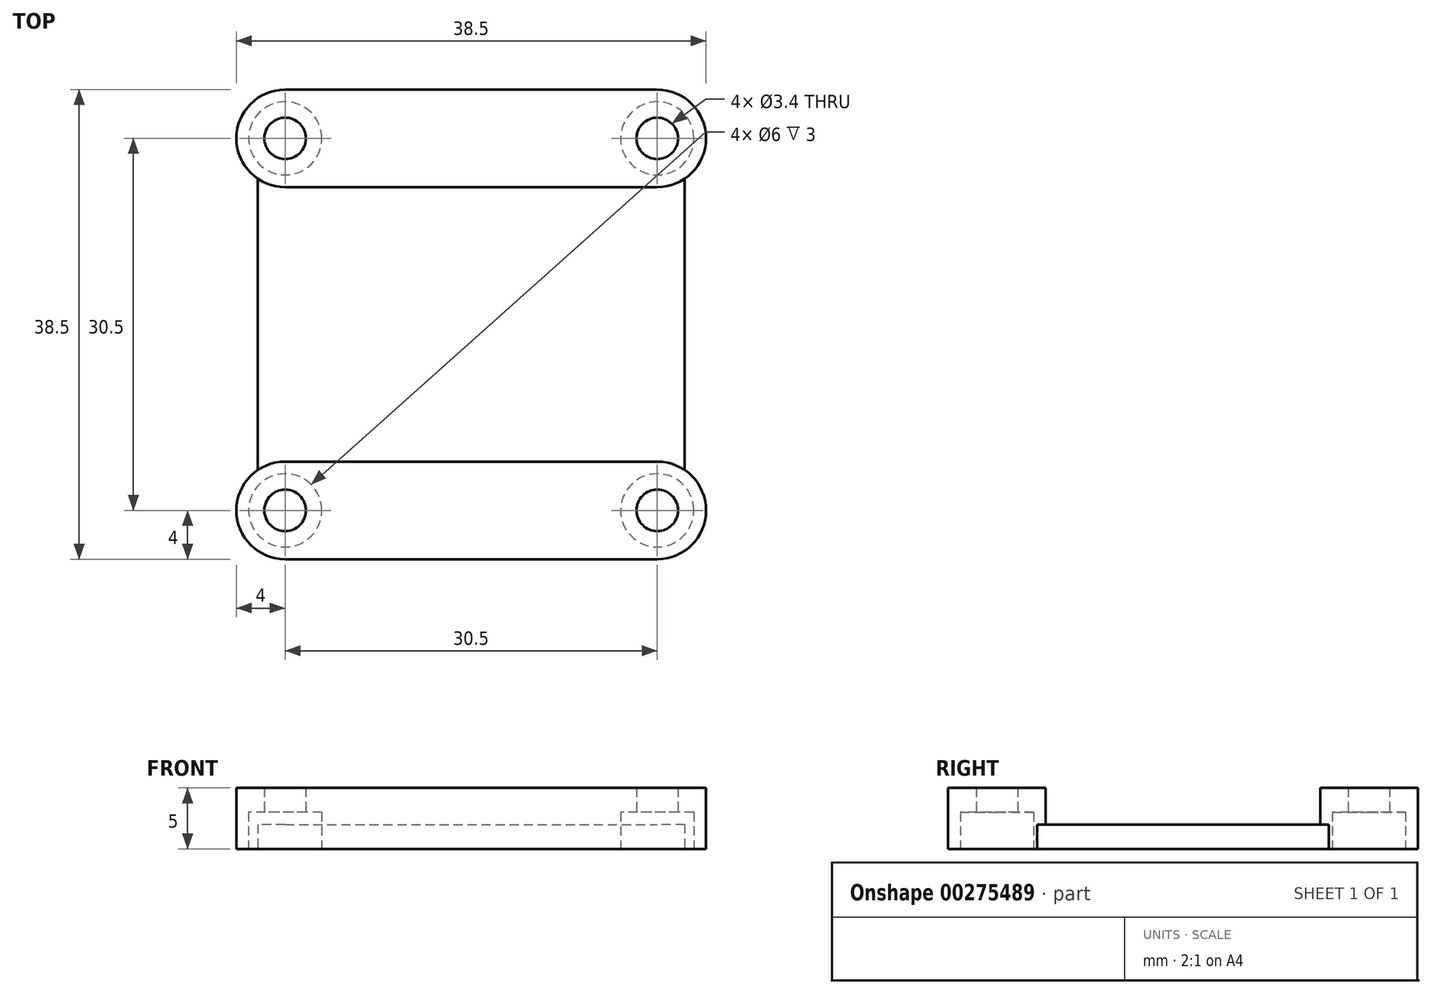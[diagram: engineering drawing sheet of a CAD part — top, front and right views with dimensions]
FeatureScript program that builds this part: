
annotation { "Feature Type Name" : "Feature", "Feature Type Description" : "" }
export const myFeature = defineFeature(function(context is Context, id is Id, definition is map)
    precondition{}
    {
        {
            var Q0;
            Q0=qCreatedBy(makeId("Top.planeOp"),FACE);
            var sketch = newSketch(context, id + "F0", { "sketchPlane" : qUnion([Q0])});
            skLineSegment(sketch, "E0.bottom", {"start": v(-19.25, -19.25) * mm, "end": v(19.25, -19.25) * mm});
            skLineSegment(sketch, "E0.top", {"start": v(-19.25, 19.25) * mm, "end": v(19.25, 19.25) * mm});
            skLineSegment(sketch, "E0.left", {"start": v(-19.25, -19.25) * mm, "end": v(-19.25, 19.25) * mm});
            skLineSegment(sketch, "E0.right", {"start": v(19.25, -19.25) * mm, "end": v(19.25, 19.25) * mm});
            skLineSegment(sketch, "E1", {"start": v(-19.25, -19.25) * mm, "end": v(19.25, 19.25) * mm, "construction": true});
            skLineSegment(sketch, "E2", {"start": v(-19.25, 19.25) * mm, "end": v(19.25, -19.25) * mm, "construction": true});
            skLineSegment(sketch, "E3", {"start": v(-19.25, 0) * mm, "end": v(19.25, 0) * mm, "construction": true});
            skLineSegment(sketch, "E4", {"start": v(0, 19.25) * mm, "end": v(0, -19.25) * mm, "construction": true});
            skCircle(sketch, "E5", {"center": v(-15.25, -15.25) * mm, "radius": 1.7 * mm});
            skCircle(sketch, "E6", {"center": v(15.25, -15.25) * mm, "radius": 1.7 * mm});
            skCircle(sketch, "E7", {"center": v(-15.25, 15.25) * mm, "radius": 1.7 * mm});
            skCircle(sketch, "E8", {"center": v(15.25, 15.25) * mm, "radius": 1.7 * mm});
            skCircle(sketch, "E9", {"center": v(15.25, 15.25) * mm, "radius": 4 * mm, "construction": true});
            skLineSegment(sketch, "E10", {"start": v(-19.25, -11.25) * mm, "end": v(19.25, -11.25) * mm});
            skLineSegment(sketch, "E11", {"start": v(-19.25, 11.25) * mm, "end": v(19.25, 11.25) * mm});
            skLineSegment(sketch, "E12", {"start": v(-17.5, -11.25) * mm, "end": v(-17.5, 11.25) * mm});
            skLineSegment(sketch, "E13", {"start": v(17.5, -11.25) * mm, "end": v(17.5, 11.25) * mm});
            skSolve(sketch);
        }
        {
            var Q0;
            {var subQ0=sQuery(id+"F0.wireOp",EDGE,"E12");Q0=makeQuery(id+"F0.imprint","IMPRINT",FACE,{"disambiguationData":[TD([[makeQuery(id+"F0.imprint","IMPRINT",EDGE,{"derivedFrom":subQ0}),-1.0]])]});}
            extrude(context, id + "F1", {"entities" : qUnion([Q0]), "depth" : 2 * mm});
        }
        {
            var Q0;
            {var subQ1=sQuery(id+"F0.wireOp",EDGE,"E0.bottom");Q0=makeQuery(id+"F0.imprint","IMPRINT",FACE,{"disambiguationData":[TD([[makeQuery(id+"F0.imprint","IMPRINT",EDGE,{"derivedFrom":subQ1}),1.0]])]});}
            var Q1;
            {var subQ1=sQuery(id+"F0.wireOp",EDGE,"E0.top");Q1=makeQuery(id+"F0.imprint","IMPRINT",FACE,{"disambiguationData":[TD([[makeQuery(id+"F0.imprint","IMPRINT",EDGE,{"derivedFrom":subQ1}),-1.0]])]});}
            extrude(context, id + "F2", {"entities" : qUnion([Q0, Q1]), "operationType" : NewBodyOperationType.ADD, "depth" : 5 * mm});
        }
        {
            var Q0;
            Q0=makeQuery(id+"F2.opExtrude","SWEPT_EDGE",EDGE,{"disambiguationData":[OSD([sQuery(id+"F0.wireOp",EDGE,"E0.bottom"),sQuery(id+"F0.wireOp",EDGE,"E0.right")])]});
            var Q1;
            Q1=makeQuery(id+"F2.opExtrude","SWEPT_EDGE",EDGE,{"disambiguationData":[OSD([sQuery(id+"F0.wireOp",EDGE,"E0.right"),sQuery(id+"F0.wireOp",EDGE,"E10")])]});
            var Q2;
            Q2=makeQuery(id+"F2.opExtrude","SWEPT_EDGE",EDGE,{"disambiguationData":[OSD([sQuery(id+"F0.wireOp",EDGE,"E0.bottom"),sQuery(id+"F0.wireOp",EDGE,"E0.left")])]});
            var Q3;
            Q3=makeQuery(id+"F2.opExtrude","SWEPT_EDGE",EDGE,{"disambiguationData":[OSD([sQuery(id+"F0.wireOp",EDGE,"E0.left"),sQuery(id+"F0.wireOp",EDGE,"E11")])]});
            var Q4;
            Q4=makeQuery(id+"F2.opExtrude","SWEPT_EDGE",EDGE,{"disambiguationData":[OSD([sQuery(id+"F0.wireOp",EDGE,"E0.right"),sQuery(id+"F0.wireOp",EDGE,"E11")])]});
            var Q5;
            Q5=makeQuery(id+"F2.opExtrude","SWEPT_EDGE",EDGE,{"disambiguationData":[OSD([sQuery(id+"F0.wireOp",EDGE,"E0.top"),sQuery(id+"F0.wireOp",EDGE,"E0.right")])]});
            var Q6;
            Q6=makeQuery(id+"F2.opExtrude","SWEPT_EDGE",EDGE,{"disambiguationData":[OSD([sQuery(id+"F0.wireOp",EDGE,"E0.left"),sQuery(id+"F0.wireOp",EDGE,"E10")])]});
            var Q7;
            Q7=makeQuery(id+"F2.opExtrude","SWEPT_EDGE",EDGE,{"disambiguationData":[OSD([sQuery(id+"F0.wireOp",EDGE,"E0.top"),sQuery(id+"F0.wireOp",EDGE,"E0.left")])]});
            fillet(context, id + "F3", {"entities" : qUnion([Q0, Q1, Q2, Q3, Q4, Q5, Q6, Q7]), "radius" : 4 * mm, "tangentPropagation" : true, "allowEdgeOverflow" : false});
        }
        {
            var Q0;
            {var subQ1=sQuery(id+"F0.wireOp",EDGE,"E0.bottom");Q0=makeQuery(id+"F0.imprint","IMPRINT",FACE,{"disambiguationData":[TD([[makeQuery(id+"F0.imprint","IMPRINT",EDGE,{"derivedFrom":subQ1}),1.0]])]});}
            var sketch = newSketch(context, id + "F4", { "sketchPlane" : qUnion([Q0])});
            skCircle(sketch, "E14", {"center": v(-15.25, -15.25) * mm, "radius": 3 * mm});
            skCircle(sketch, "E15", {"center": v(15.25, -15.25) * mm, "radius": 3 * mm});
            skCircle(sketch, "E16", {"center": v(15.25, 15.25) * mm, "radius": 3 * mm});
            skCircle(sketch, "E17", {"center": v(-15.25, 15.25) * mm, "radius": 3 * mm});
            skSolve(sketch);
        }
        {
            var Q0;
            Q0 = qSketchRegion(id + "F4", true);
            extrude(context, id + "F5", {"entities" : qUnion([Q0]), "operationType" : NewBodyOperationType.REMOVE, "depth" : 3 * mm});
        }
    });
